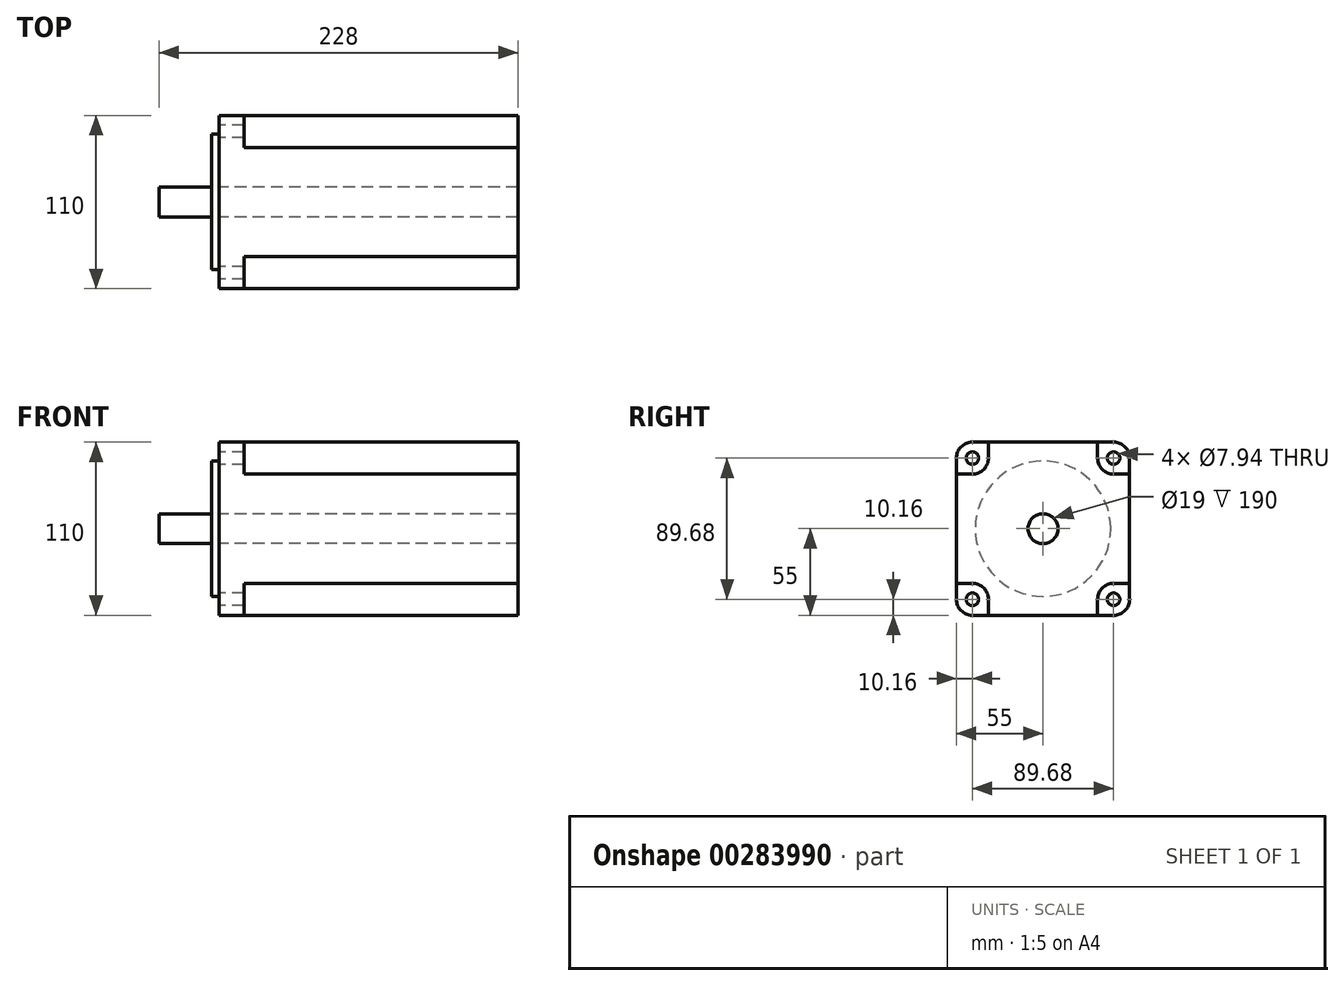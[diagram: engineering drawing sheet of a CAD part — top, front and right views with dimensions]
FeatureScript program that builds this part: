
annotation { "Feature Type Name" : "Feature", "Feature Type Description" : "" }
export const myFeature = defineFeature(function(context is Context, id is Id, definition is map)
    precondition{}
    {
        {
            var Q0;
            Q0=qCreatedBy(makeId("Right.planeOp"),FACE);
            var sketch = newSketch(context, id + "F0", { "sketchPlane" : qUnion([Q0])});
            skLineSegment(sketch, "E0.bottom", {"start": v(44.84, -55) * mm, "end": v(-44.84, -55) * mm});
            skLineSegment(sketch, "E0.top", {"start": v(44.84, 55) * mm, "end": v(-44.84, 55) * mm});
            skLineSegment(sketch, "E0.left", {"start": v(55, -44.84) * mm, "end": v(55, 44.84) * mm});
            skLineSegment(sketch, "E0.right", {"start": v(-55, -44.84) * mm, "end": v(-55, 44.84) * mm});
            skPoint(sketch, "E0.middle", {"position": v(0, 0) * mm});
            skCircle(sketch, "E1", {"center": v(0, 0) * mm, "radius": 9.5 * mm});
            skPoint(sketch, "E2.visualSharp", {"position": v(-55, 55) * mm});
            skArc(sketch, "E2.filletArc", {"start": v(-44.84, 55) * mm, "mid": v(-52.02, 52.02) * mm, "end": v(-55, 44.84) * mm});
            skPoint(sketch, "E3.visualSharp", {"position": v(55, 55) * mm});
            skArc(sketch, "E3.filletArc", {"start": v(55, 44.84) * mm, "mid": v(52.02, 52.02) * mm, "end": v(44.84, 55) * mm});
            skPoint(sketch, "E4.visualSharp", {"position": v(55, -55) * mm});
            skArc(sketch, "E4.filletArc", {"start": v(44.84, -55) * mm, "mid": v(52.02, -52.02) * mm, "end": v(55, -44.84) * mm});
            skPoint(sketch, "E5.visualSharp", {"position": v(-55, -55) * mm});
            skArc(sketch, "E5.filletArc", {"start": v(-55, -44.84) * mm, "mid": v(-52.02, -52.02) * mm, "end": v(-44.84, -55) * mm});
            skPoint(sketch, "E6.visualSharp", {"position": v(-52, 52) * mm});
            skPoint(sketch, "E7.visualSharp", {"position": v(52, 52) * mm});
            skPoint(sketch, "E8.visualSharp", {"position": v(52, -52) * mm});
            skPoint(sketch, "E9.visualSharp", {"position": v(-52, -52) * mm});
            skCircle(sketch, "E10", {"center": v(0, 0) * mm, "radius": 43 * mm});
            skLineSegment(sketch, "E11", {"start": v(-34.68, -55) * mm, "end": v(-34.68, -44.84) * mm});
            skLineSegment(sketch, "E12", {"start": v(-44.84, -34.68) * mm, "end": v(-55, -34.68) * mm});
            skLineSegment(sketch, "E13", {"start": v(-34.68, 55) * mm, "end": v(-34.68, 44.84) * mm});
            skLineSegment(sketch, "E14", {"start": v(-44.84, 34.68) * mm, "end": v(-55, 34.68) * mm});
            skLineSegment(sketch, "E15", {"start": v(34.68, 55) * mm, "end": v(34.68, 44.84) * mm});
            skLineSegment(sketch, "E16", {"start": v(44.84, 34.68) * mm, "end": v(55, 34.68) * mm});
            skLineSegment(sketch, "E17", {"start": v(34.68, -55) * mm, "end": v(34.68, -44.84) * mm});
            skLineSegment(sketch, "E18", {"start": v(44.84, -34.68) * mm, "end": v(55, -34.68) * mm});
            skCircle(sketch, "E19", {"center": v(44.84, 44.84) * mm, "radius": 3.97 * mm});
            skCircle(sketch, "E20", {"center": v(44.84, -44.84) * mm, "radius": 3.97 * mm});
            skPoint(sketch, "E21.visualSharp", {"position": v(-34.68, 34.68) * mm});
            skArc(sketch, "E21.filletArc", {"start": v(-44.84, 34.68) * mm, "mid": v(-37.66, 37.66) * mm, "end": v(-34.68, 44.84) * mm});
            skPoint(sketch, "E22.visualSharp", {"position": v(34.68, 34.68) * mm});
            skArc(sketch, "E22.filletArc", {"start": v(34.68, 44.84) * mm, "mid": v(37.66, 37.66) * mm, "end": v(44.84, 34.68) * mm});
            skPoint(sketch, "E23.visualSharp", {"position": v(34.68, -34.68) * mm});
            skArc(sketch, "E23.filletArc", {"start": v(44.84, -34.68) * mm, "mid": v(37.66, -37.66) * mm, "end": v(34.68, -44.84) * mm});
            skPoint(sketch, "E24.visualSharp", {"position": v(-34.68, -34.68) * mm});
            skArc(sketch, "E24.filletArc", {"start": v(-34.68, -44.84) * mm, "mid": v(-37.66, -37.66) * mm, "end": v(-44.84, -34.68) * mm});
            skCircle(sketch, "E25", {"center": v(-44.84, 44.84) * mm, "radius": 3.97 * mm});
            skCircle(sketch, "E26", {"center": v(-44.84, -44.84) * mm, "radius": 3.97 * mm});
            skSolve(sketch);
        }
        {
            var Q0;
            Q0=makeQuery(id+"F0.imprint","IMPRINT",FACE,{"disambiguationData":[TD([[makeQuery(id+"F0.imprint","IMPRINT",EDGE,{"derivedFrom":sQuery(id+"F0.wireOp",EDGE,"E1")}),1.0]])]});
            extrude(context, id + "F1", {"entities" : qUnion([Q0]), "oppositeDirection" : true, "depth" : 38 * mm});
        }
        {
            var Q0;
            Q0=makeQuery(id+"F0.imprint","IMPRINT",FACE,{"disambiguationData":[TD([[makeQuery(id+"F0.imprint","IMPRINT",EDGE,{"derivedFrom":sQuery(id+"F0.wireOp",EDGE,"E1")}),-1.0]])]});
            extrude(context, id + "F2", {"entities" : qUnion([Q0]), "operationType" : NewBodyOperationType.ADD, "oppositeDirection" : true, "depth" : 0.12 * 38 * mm});
        }
        {
            var Q0;
            Q0=makeQuery(id+"F0.imprint","IMPRINT",FACE,{"disambiguationData":[TD([[makeQuery(id+"F0.imprint","IMPRINT",EDGE,{"derivedFrom":sQuery(id+"F0.wireOp",EDGE,"E1")}),-1.0]])]});
            var Q1;
            Q1=makeQuery(id+"F0.imprint","IMPRINT",FACE,{"disambiguationData":[TD([[makeQuery(id+"F0.imprint","IMPRINT",EDGE,{"derivedFrom":sQuery(id+"F0.wireOp",EDGE,"E10")}),-1.0]])]});
            extrude(context, id + "F3", {"entities" : qUnion([Q0, Q1]), "operationType" : NewBodyOperationType.ADD, "depth" : 190 * mm});
        }
        {
            var Q0;
            {var subQ0=sQuery(id+"F0.wireOp",EDGE,"E2.filletArc");Q0=makeQuery(id+"F0.imprint","IMPRINT",FACE,{"disambiguationData":[TD([[makeQuery(id+"F0.imprint","IMPRINT",EDGE,{"derivedFrom":subQ0}),1.0]])]});}
            var Q1;
            {var subQ1=sQuery(id+"F0.wireOp",EDGE,"E3.filletArc");Q1=makeQuery(id+"F0.imprint","IMPRINT",FACE,{"disambiguationData":[TD([[makeQuery(id+"F0.imprint","IMPRINT",EDGE,{"derivedFrom":subQ1}),1.0]])]});}
            var Q2;
            {var subQ1=sQuery(id+"F0.wireOp",EDGE,"E4.filletArc");Q2=makeQuery(id+"F0.imprint","IMPRINT",FACE,{"disambiguationData":[TD([[makeQuery(id+"F0.imprint","IMPRINT",EDGE,{"derivedFrom":subQ1}),1.0]])]});}
            var Q3;
            {var subQ1=sQuery(id+"F0.wireOp",EDGE,"E5.filletArc");Q3=makeQuery(id+"F0.imprint","IMPRINT",FACE,{"disambiguationData":[TD([[makeQuery(id+"F0.imprint","IMPRINT",EDGE,{"derivedFrom":subQ1}),1.0]])]});}
            extrude(context, id + "F4", {"entities" : qUnion([Q0, Q1, Q2, Q3]), "operationType" : NewBodyOperationType.ADD, "depth" : 15.88 * mm});
        }
    });
